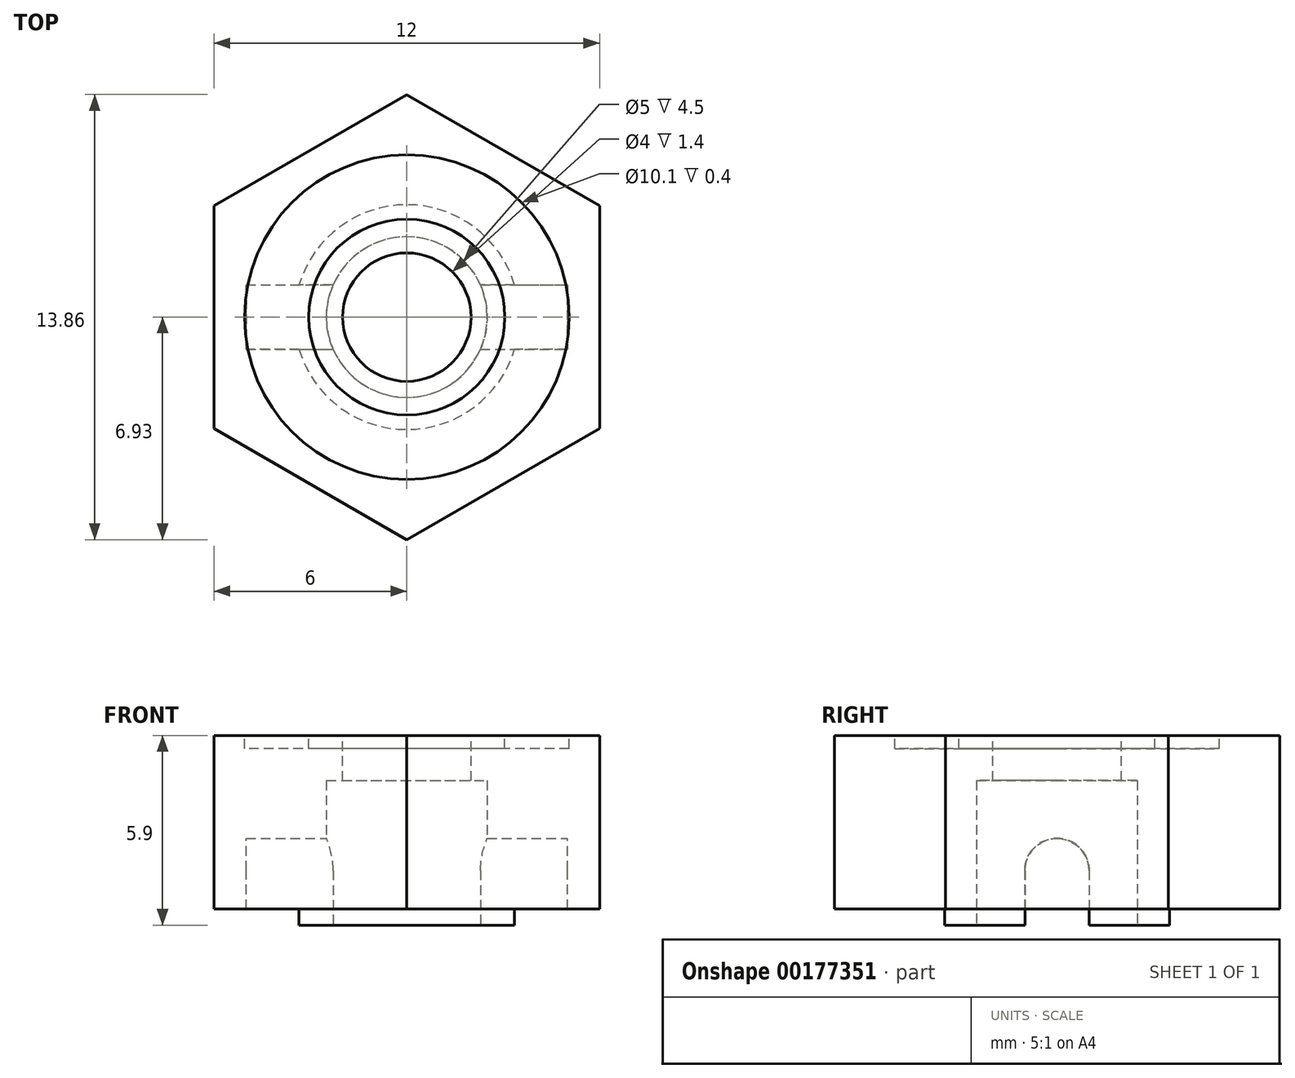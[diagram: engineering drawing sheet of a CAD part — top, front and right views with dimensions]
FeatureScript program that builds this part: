
annotation { "Feature Type Name" : "Feature", "Feature Type Description" : "" }
export const myFeature = defineFeature(function(context is Context, id is Id, definition is map)
    precondition{}
    {
        {
            var Q0;
            Q0=qCreatedBy(makeId("Top.planeOp"),FACE);
            var sketch = newSketch(context, id + "F0", { "sketchPlane" : qUnion([Q0])});
            skCircle(sketch, "E0.cCircle", {"center": v(0, 0) * mm, "radius": 6 * mm, "construction": true});
            skLineSegment(sketch, "E0.0", {"start": v(6, 3.46) * mm, "end": v(6, -3.46) * mm});
            skLineSegment(sketch, "E0.1", {"start": v(6, -3.46) * mm, "end": v(0, -6.93) * mm});
            skLineSegment(sketch, "E0.2", {"start": v(0, -6.93) * mm, "end": v(-6, -3.46) * mm});
            skLineSegment(sketch, "E0.3", {"start": v(-6, -3.46) * mm, "end": v(-6, 3.46) * mm});
            skLineSegment(sketch, "E0.4", {"start": v(-6, 3.46) * mm, "end": v(0, 6.93) * mm});
            skLineSegment(sketch, "E0.5", {"start": v(0, 6.93) * mm, "end": v(6, 3.46) * mm});
            skPoint(sketch, "E0.0.midPoint", {"position": v(6, 0) * mm});
            skSolve(sketch);
        }
        {
            var Q0;
            Q0 = qSketchRegion(id + "F0", true);
            extrude(context, id + "F1", {"entities" : qUnion([Q0]), "depth" : 5.4 * mm, "offsetDistance" : 25 * mm});
        }
        {
            var Q0;
            Q0=makeQuery(id+"F1.opExtrude","CAP_FACE",FACE,{"disambiguationData":[OSD([sQuery(id+"F0.wireOp",EDGE,"E0.0"),sQuery(id+"F0.wireOp",EDGE,"E0.1"),sQuery(id+"F0.wireOp",EDGE,"E0.2"),sQuery(id+"F0.wireOp",EDGE,"E0.3"),sQuery(id+"F0.wireOp",EDGE,"E0.4"),sQuery(id+"F0.wireOp",EDGE,"E0.5")])],"isStart":false});
            var sketch = newSketch(context, id + "F2", { "sketchPlane" : qUnion([Q0])});
            skCircle(sketch, "E1", {"center": v(0, 0) * mm, "radius": 5.05 * mm});
            skCircle(sketch, "E2", {"center": v(0, 0) * mm, "radius": 3.05 * mm});
            skSolve(sketch);
        }
        {
            var Q0;
            Q0 = qSketchRegion(id + "F2", true);
            extrude(context, id + "F3", {"entities" : qUnion([Q0]), "operationType" : NewBodyOperationType.REMOVE, "oppositeDirection" : true, "depth" : 0.4 * mm, "offsetDistance" : 25 * mm});
        }
        {
            var Q0;
            Q0=makeQuery(id+"F3.boolean.opBoolean","SPLIT",FACE,{"disambiguationData":[TD([makeQuery(id+"F3.opExtrude","SWEPT_FACE",FACE,{"disambiguationData":[OSD([sQuery(id+"F2.wireOp",EDGE,"E2")])]})])],"derivedFrom":makeQuery(id+"F1.opExtrude","CAP_FACE",FACE,{"disambiguationData":[OSD([sQuery(id+"F0.wireOp",EDGE,"E0.0"),sQuery(id+"F0.wireOp",EDGE,"E0.1"),sQuery(id+"F0.wireOp",EDGE,"E0.2"),sQuery(id+"F0.wireOp",EDGE,"E0.3"),sQuery(id+"F0.wireOp",EDGE,"E0.4"),sQuery(id+"F0.wireOp",EDGE,"E0.5")])],"isStart":false})});
            var sketch = newSketch(context, id + "F4", { "sketchPlane" : qUnion([Q0])});
            skCircle(sketch, "E3", {"center": v(0, 0) * mm, "radius": 2 * mm});
            skSolve(sketch);
        }
        {
            var Q0;
            Q0 = qSketchRegion(id + "F4", true);
            extrude(context, id + "F5", {"entities" : qUnion([Q0]), "operationType" : NewBodyOperationType.REMOVE, "endBound" : BoundingType.THROUGH_ALL, "oppositeDirection" : true, "depth" : 25 * mm, "offsetDistance" : 25 * mm});
        }
        {
            var Q0;
            Q0=makeQuery(id+"F1.opExtrude","CAP_FACE",FACE,{"disambiguationData":[OSD([sQuery(id+"F0.wireOp",EDGE,"E0.0"),sQuery(id+"F0.wireOp",EDGE,"E0.1"),sQuery(id+"F0.wireOp",EDGE,"E0.2"),sQuery(id+"F0.wireOp",EDGE,"E0.3"),sQuery(id+"F0.wireOp",EDGE,"E0.4"),sQuery(id+"F0.wireOp",EDGE,"E0.5")])],"isStart":true});
            var sketch = newSketch(context, id + "F6", { "sketchPlane" : qUnion([Q0])});
            skCircle(sketch, "E4", {"center": v(0, 0) * mm, "radius": 2 * mm});
            skCircle(sketch, "E5", {"center": v(0, 0) * mm, "radius": 3.5 * mm});
            skSolve(sketch);
        }
        {
            var Q0;
            Q0 = qSketchRegion(id + "F6", true);
            extrude(context, id + "F7", {"entities" : qUnion([Q0]), "operationType" : NewBodyOperationType.ADD, "depth" : 0.5 * mm, "offsetDistance" : 25 * mm});
        }
        {
            var Q0;
            Q0=makeQuery(id+"F7.opExtrude","CAP_FACE",FACE,{"disambiguationData":[OSD([sQuery(id+"F6.wireOp",EDGE,"E4"),sQuery(id+"F6.wireOp",EDGE,"E5")])],"isStart":false});
            var sketch = newSketch(context, id + "F8", { "sketchPlane" : qUnion([Q0])});
            skCircle(sketch, "E6", {"center": v(0, 0) * mm, "radius": 2.5 * mm});
            skSolve(sketch);
        }
        {
            var Q0;
            Q0 = qSketchRegion(id + "F8", true);
            extrude(context, id + "F9", {"entities" : qUnion([Q0]), "operationType" : NewBodyOperationType.REMOVE, "oppositeDirection" : true, "depth" : 4.5 * mm, "offsetDistance" : 25 * mm});
        }
        {
            var Q0;
            Q0=qCreatedBy(makeId("Right.planeOp"),FACE);
            var sketch = newSketch(context, id + "F10", { "sketchPlane" : qUnion([Q0])});
            skArc(sketch, "E7", {"start": v(1, 1.2) * mm, "mid": v(0, 2.2) * mm, "end": v(-1, 1.2) * mm});
            skLineSegment(sketch, "E8", {"start": v(1, 1.2) * mm, "end": v(1, -1.5) * mm});
            skLineSegment(sketch, "E9", {"start": v(1, -1.5) * mm, "end": v(-1, -1.5) * mm});
            skLineSegment(sketch, "E10", {"start": v(-1, -1.5) * mm, "end": v(-1, 1.2) * mm});
            skSolve(sketch);
        }
        {
            var Q0;
            Q0 = qSketchRegion(id + "F10", true);
            extrude(context, id + "F11", {"entities" : qUnion([Q0]), "operationType" : NewBodyOperationType.REMOVE, "oppositeDirection" : true, "depth" : 10 * mm, "offsetDistance" : 25 * mm, "symmetric" : true});
        }
    });
